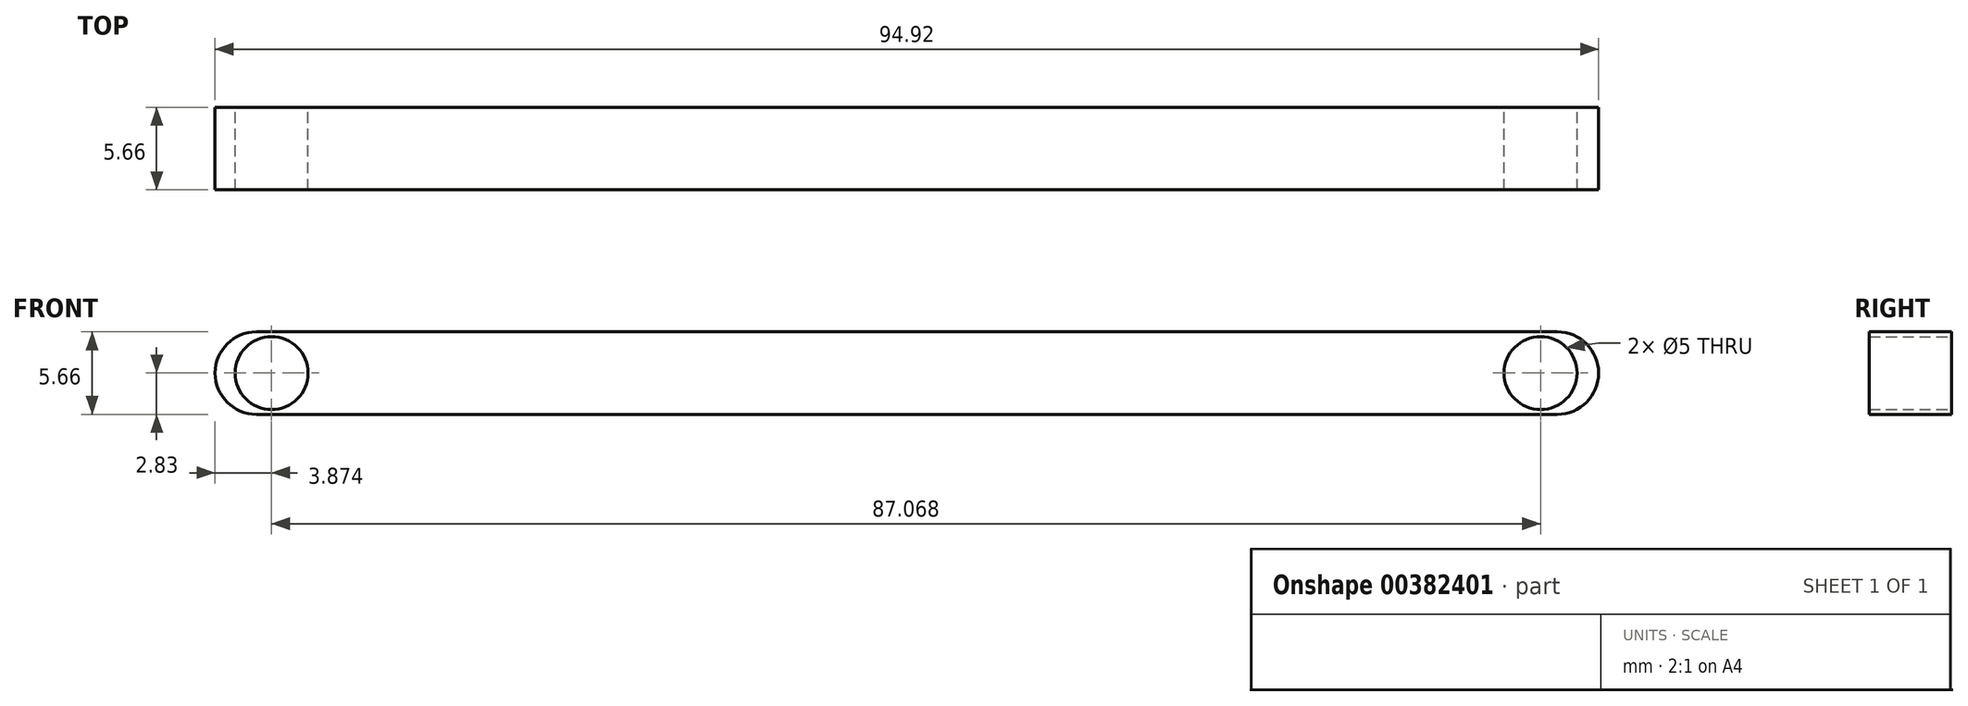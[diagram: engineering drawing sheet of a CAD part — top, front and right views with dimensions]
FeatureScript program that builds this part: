
annotation { "Feature Type Name" : "Feature", "Feature Type Description" : "" }
export const myFeature = defineFeature(function(context is Context, id is Id, definition is map)
    precondition{}
    {
        {
            var Q0;
            Q0=qCreatedBy(makeId("Front.planeOp"),FACE);
            var sketch = newSketch(context, id + "F0", { "sketchPlane" : qUnion([Q0])});
            skLineSegment(sketch, "E0.bottom", {"start": v(44.63, -2.83) * mm, "end": v(-44.63, -2.83) * mm});
            skLineSegment(sketch, "E0.top", {"start": v(44.63, 2.83) * mm, "end": v(-44.63, 2.83) * mm});
            skPoint(sketch, "E0.middle", {"position": v(0, 0) * mm});
            skArc(sketch, "E1", {"start": v(-44.63, 2.83) * mm, "mid": v(-47.46, 0) * mm, "end": v(-44.63, -2.83) * mm});
            skArc(sketch, "E2", {"start": v(44.63, -2.83) * mm, "mid": v(47.46, 0) * mm, "end": v(44.63, 2.83) * mm});
            skCircle(sketch, "E3", {"center": v(-43.59, 0) * mm, "radius": 2.5 * mm});
            skCircle(sketch, "E4", {"center": v(43.48, 0) * mm, "radius": 2.5 * mm});
            skSolve(sketch);
        }
        {
            var Q0;
            Q0=makeQuery(id+"F0.imprint","IMPRINT",FACE,{"disambiguationData":[TD([[makeQuery(id+"F0.imprint","IMPRINT",EDGE,{"derivedFrom":sQuery(id+"F0.wireOp",EDGE,"E0.bottom")}),-1.0]])]});
            extrude(context, id + "F1", {"entities" : qUnion([Q0]), "depth" : 5.66 * mm});
        }
    });
